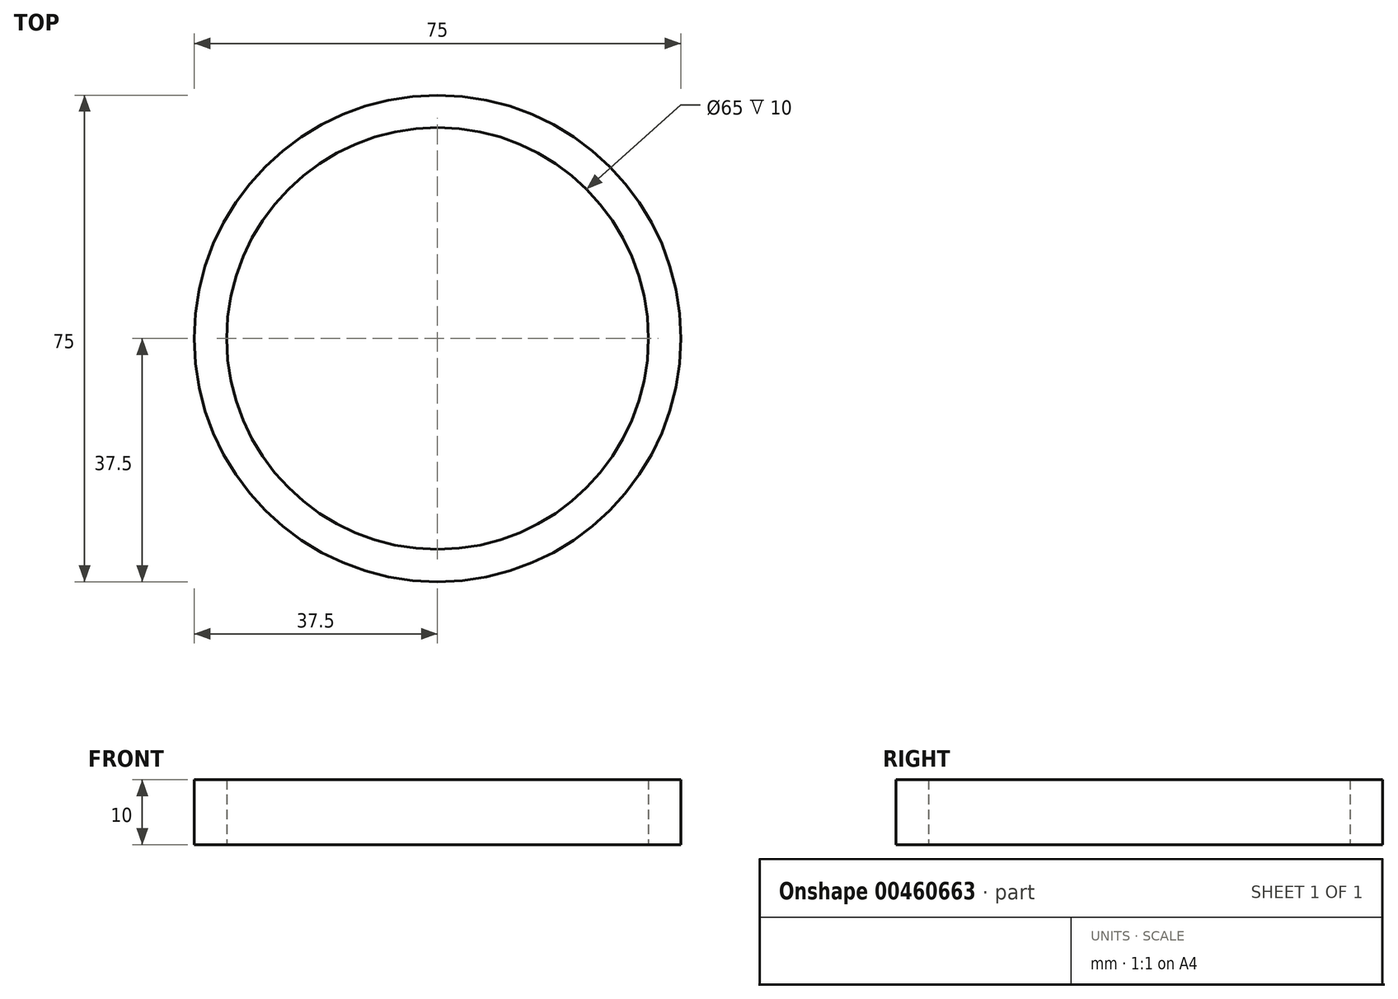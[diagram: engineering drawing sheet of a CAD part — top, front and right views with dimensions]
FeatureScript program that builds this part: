
annotation { "Feature Type Name" : "Feature", "Feature Type Description" : "" }
export const myFeature = defineFeature(function(context is Context, id is Id, definition is map)
    precondition{}
    {
        {
            var Q0;
            Q0=qCreatedBy(makeId("Front.planeOp"),FACE);
            var sketch = newSketch(context, id + "F0", { "sketchPlane" : qUnion([Q0])});
            skLineSegment(sketch, "E0", {"start": v(0, 0) * mm, "end": v(0, 210) * mm, "construction": true});
            skLineSegment(sketch, "E1.bottom", {"start": v(-37.5, 0) * mm, "end": v(-32.5, 0) * mm});
            skLineSegment(sketch, "E1.top", {"start": v(-37.5, 10) * mm, "end": v(-32.5, 10) * mm});
            skLineSegment(sketch, "E1.left", {"start": v(-37.5, 0) * mm, "end": v(-37.5, 10) * mm});
            skLineSegment(sketch, "E1.right", {"start": v(-32.5, 0) * mm, "end": v(-32.5, 10) * mm});
            skSolve(sketch);
        }
        {
            var Q0;
            Q0=makeQuery(id+"F0.imprint","IMPRINT",FACE,{"disambiguationData":[TD([[makeQuery(id+"F0.imprint","IMPRINT",EDGE,{"derivedFrom":sQuery(id+"F0.wireOp",EDGE,"E1.bottom")}),1.0]])]});
            var Q1;
            Q1=sQuery(id+"F0.wireOp",EDGE,"E0");
            revolve(context, id + "F1", {"entities" : qUnion([Q0]), "axis" : qUnion([Q1]), "revolveType" : RevolveType.FULL});
        }
    });
